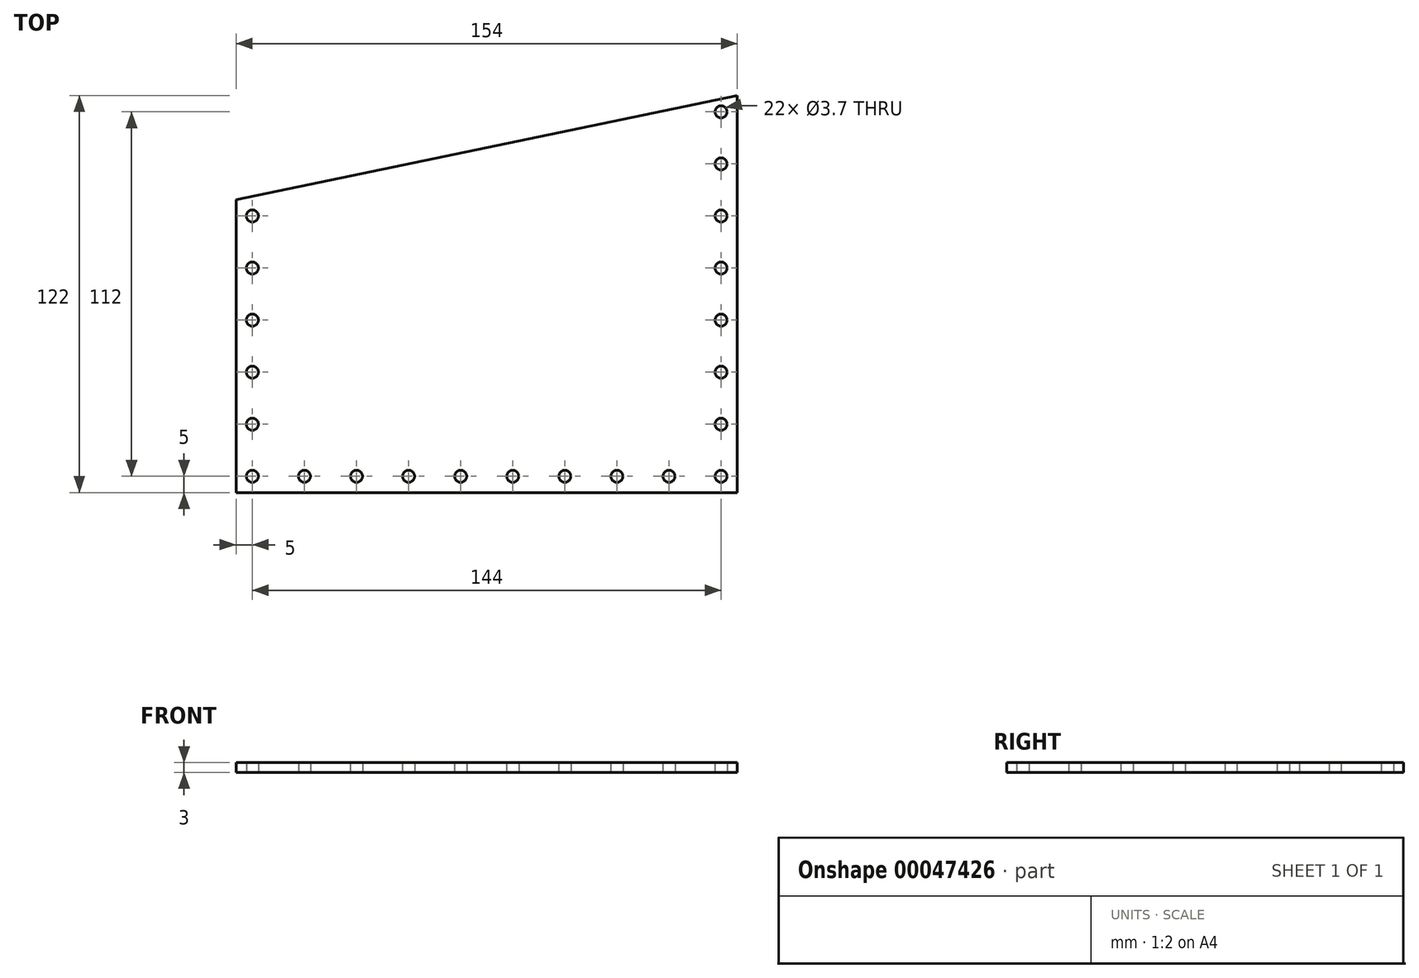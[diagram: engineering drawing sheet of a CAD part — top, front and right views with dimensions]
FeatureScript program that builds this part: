
annotation { "Feature Type Name" : "Feature", "Feature Type Description" : "" }
export const myFeature = defineFeature(function(context is Context, id is Id, definition is map)
    precondition{}
    {
        {
            var Q0;
            Q0=qCreatedBy(makeId("Top.planeOp"),FACE);
            var sketch = newSketch(context, id + "F0", { "sketchPlane" : qUnion([Q0])});
            skLineSegment(sketch, "E0.rect.bottom", {"start": v(-72, -54.5) * mm, "end": v(82, -54.5) * mm});
            skPoint(sketch, "E0.rect.middle", {"position": v(0, 0) * mm});
            skLineSegment(sketch, "E1", {"start": v(-72, -54.5) * mm, "end": v(-72, 35.5) * mm});
            skLineSegment(sketch, "E2", {"start": v(82, -54.5) * mm, "end": v(82, 67.5) * mm});
            skLineSegment(sketch, "E3", {"start": v(82, 67.5) * mm, "end": v(-72, 35.5) * mm});
            skLineSegment(sketch, "E4.bottom", {"start": v(-72, -54.5) * mm, "end": v(-67, -54.5) * mm, "construction": true});
            skLineSegment(sketch, "E4.top", {"start": v(-72, -49.5) * mm, "end": v(-67, -49.5) * mm, "construction": true});
            skLineSegment(sketch, "E4.left", {"start": v(-72, -54.5) * mm, "end": v(-72, -49.5) * mm, "construction": true});
            skLineSegment(sketch, "E4.right", {"start": v(-67, -54.5) * mm, "end": v(-67, -49.5) * mm, "construction": true});
            skCircle(sketch, "E5", {"center": v(-67, -49.5) * mm, "radius": 1.85 * mm});
            skCircle(sketch, "E6.1.0.0", {"center": v(-51, -49.5) * mm, "radius": 1.85 * mm});
            skCircle(sketch, "E6.2.0.0", {"center": v(-35, -49.5) * mm, "radius": 1.85 * mm});
            skCircle(sketch, "E6.3.0.0", {"center": v(-19, -49.5) * mm, "radius": 1.85 * mm});
            skCircle(sketch, "E6.4.0.0", {"center": v(-3, -49.5) * mm, "radius": 1.85 * mm});
            skCircle(sketch, "E6.5.0.0", {"center": v(13, -49.5) * mm, "radius": 1.85 * mm});
            skCircle(sketch, "E6.6.0.0", {"center": v(29, -49.5) * mm, "radius": 1.85 * mm});
            skCircle(sketch, "E6.7.0.0", {"center": v(45, -49.5) * mm, "radius": 1.85 * mm});
            skCircle(sketch, "E6.8.0.0", {"center": v(61, -49.5) * mm, "radius": 1.85 * mm});
            skLineSegment(sketch, "E6.direction1", {"start": v(-67, -49.5) * mm, "end": v(-51, -49.5) * mm, "construction": true});
            skCircle(sketch, "E7.0.9.0", {"center": v(77, -49.5) * mm, "radius": 1.85 * mm});
            skCircle(sketch, "E8.0.1.0", {"center": v(-67, -33.5) * mm, "radius": 1.85 * mm});
            skCircle(sketch, "E8.0.2.0", {"center": v(-67, -17.5) * mm, "radius": 1.85 * mm});
            skCircle(sketch, "E8.0.3.0", {"center": v(-67, -1.5) * mm, "radius": 1.85 * mm});
            skCircle(sketch, "E8.0.4.0", {"center": v(-67, 14.5) * mm, "radius": 1.85 * mm});
            skCircle(sketch, "E8.0.5.0", {"center": v(-67, 30.5) * mm, "radius": 1.85 * mm});
            skLineSegment(sketch, "E8.direction1", {"start": v(-67, -49.5) * mm, "end": v(-42, -49.5) * mm, "construction": true});
            skLineSegment(sketch, "E8.direction2", {"start": v(-67, -49.5) * mm, "end": v(-67, -33.5) * mm, "construction": true});
            skCircle(sketch, "E9.0.1.0", {"center": v(77, -33.5) * mm, "radius": 1.85 * mm});
            skCircle(sketch, "E9.0.2.0", {"center": v(77, -17.5) * mm, "radius": 1.85 * mm});
            skCircle(sketch, "E9.0.3.0", {"center": v(77, -1.5) * mm, "radius": 1.85 * mm});
            skCircle(sketch, "E9.0.4.0", {"center": v(77, 14.5) * mm, "radius": 1.85 * mm});
            skCircle(sketch, "E9.0.5.0", {"center": v(77, 30.5) * mm, "radius": 1.85 * mm});
            skCircle(sketch, "E9.0.6.0", {"center": v(77, 46.5) * mm, "radius": 1.85 * mm});
            skCircle(sketch, "E9.0.7.0", {"center": v(77, 62.5) * mm, "radius": 1.85 * mm});
            skLineSegment(sketch, "E9.direction1", {"start": v(77, -49.5) * mm, "end": v(102, -49.5) * mm, "construction": true});
            skLineSegment(sketch, "E9.direction2", {"start": v(77, -49.5) * mm, "end": v(77, -33.5) * mm, "construction": true});
            skSolve(sketch);
        }
        {
            var Q0;
            Q0=makeQuery(id+"F0.imprint","IMPRINT",FACE,{"disambiguationData":[TD([[makeQuery(id+"F0.imprint","IMPRINT",EDGE,{"derivedFrom":sQuery(id+"F0.wireOp",EDGE,"E0.rect.bottom")}),1.0]])]});
            extrude(context, id + "F1", {"entities" : qUnion([Q0]), "depth" : 3 * mm});
        }
    });
